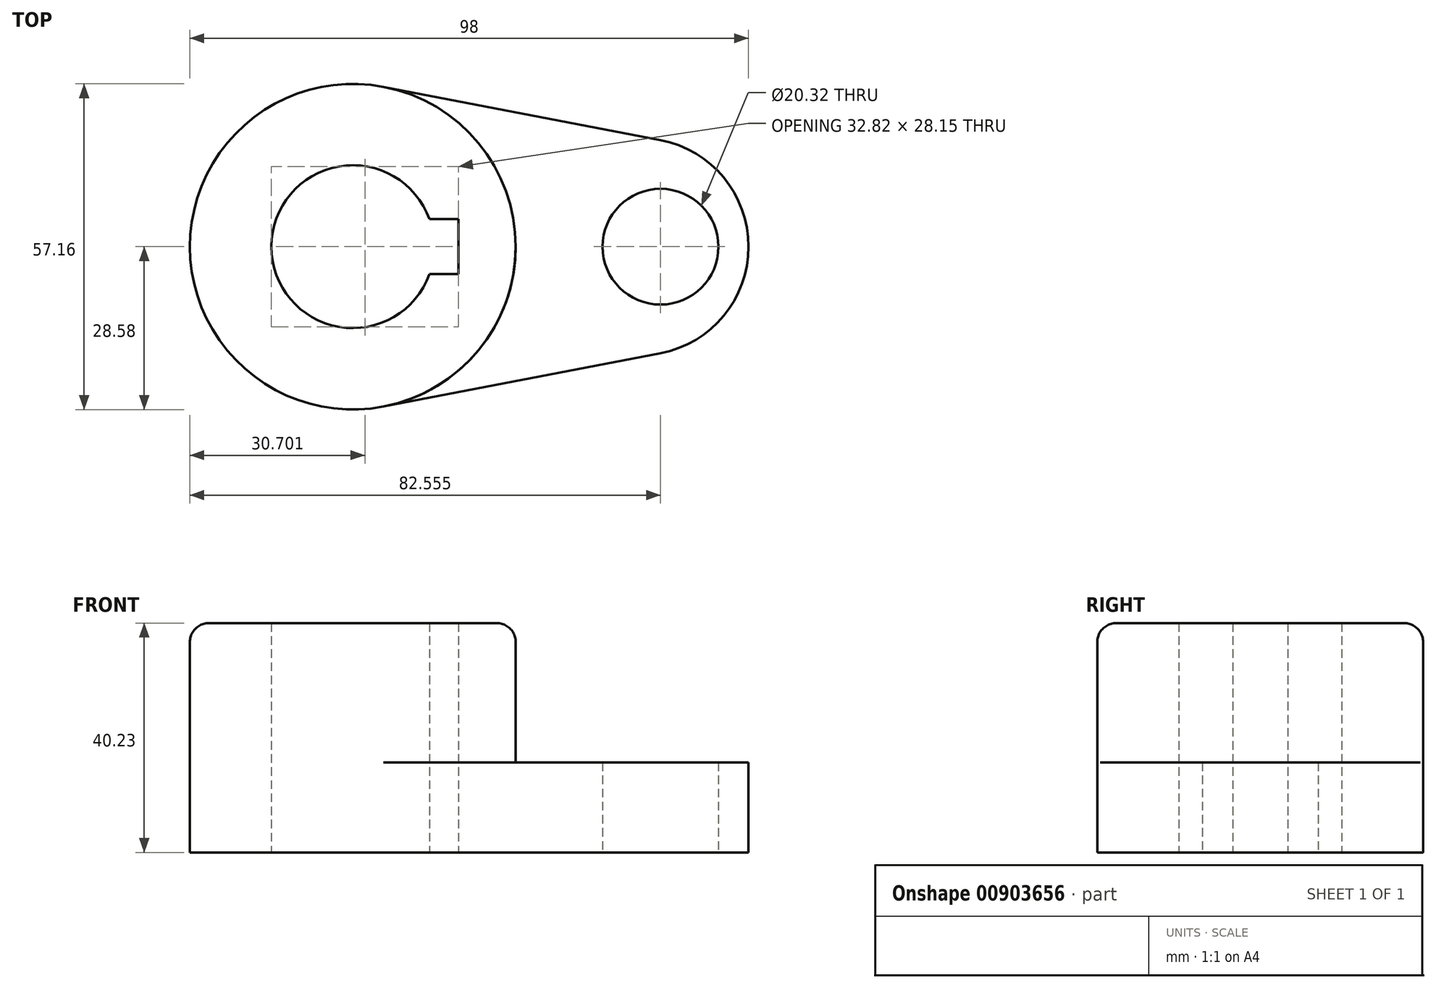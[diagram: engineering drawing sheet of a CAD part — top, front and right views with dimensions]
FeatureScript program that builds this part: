
annotation { "Feature Type Name" : "Feature", "Feature Type Description" : "" }
export const myFeature = defineFeature(function(context is Context, id is Id, definition is map)
    precondition{}
    {
        {
            var Q0;
            Q0=qCreatedBy(makeId("Top.planeOp"),FACE);
            var sketch = newSketch(context, id + "F0", { "sketchPlane" : qUnion([Q0])});
            skCircle(sketch, "E0", {"center": v(0, 0) * mm, "radius": 28.58 * mm});
            skCircle(sketch, "E1", {"center": v(53.98, 0) * mm, "radius": 10.16 * mm});
            skArc(sketch, "E2", {"start": v(13.45, 4.83) * mm, "mid": v(-14.29, 0) * mm, "end": v(13.45, -4.83) * mm});
            skLineSegment(sketch, "E3", {"start": v(14.29, 0) * mm, "end": v(18.53, 0) * mm});
            skLineSegment(sketch, "E4.bottom", {"start": v(18.53, 4.83) * mm, "end": v(13.45, 4.83) * mm});
            skLineSegment(sketch, "E4.top", {"start": v(18.53, -4.83) * mm, "end": v(13.45, -4.83) * mm});
            skLineSegment(sketch, "E4.left", {"start": v(18.53, 4.83) * mm, "end": v(18.53, -4.83) * mm});
            skPoint(sketch, "E4.middle", {"position": v(14.29, 0) * mm});
            skPoint(sketch, "E5.orphan", {"position": v(10.05, -4.83) * mm});
            skPoint(sketch, "E6.orphan", {"position": v(10.05, 4.83) * mm});
            skLineSegment(sketch, "E7", {"start": v(53.97, -18.7) * mm, "end": v(5.4, -28.06) * mm});
            skLineSegment(sketch, "E8", {"start": v(5.4, 28.06) * mm, "end": v(53.98, 18.7) * mm});
            skArc(sketch, "E9", {"start": v(53.97, -18.7) * mm, "mid": v(69.42, 0) * mm, "end": v(53.97, 18.7) * mm});
            skSolve(sketch);
        }
        {
            var Q0;
            Q0=makeQuery(id+"F0.imprint","IMPRINT",FACE,{"disambiguationData":[TD([[makeQuery(id+"F0.imprint","IMPRINT",EDGE,{"derivedFrom":sQuery(id+"F0.wireOp",EDGE,"E1")}),-1.0]])]});
            extrude(context, id + "F1", {"entities" : qUnion([Q0]), "depth" : 15.77 * mm, "offsetDistance" : 25.4 * mm});
        }
        {
            var Q0;
            Q0=makeQuery(id+"F0.imprint","IMPRINT",FACE,{"disambiguationData":[TD([[makeQuery(id+"F0.imprint","IMPRINT",EDGE,{"derivedFrom":sQuery(id+"F0.wireOp",EDGE,"E2")}),-1.0]])]});
            extrude(context, id + "F2", {"entities" : qUnion([Q0]), "operationType" : NewBodyOperationType.ADD, "depth" : 40.23 * mm, "offsetDistance" : 25.4 * mm});
        }
        {
            var Q0;
            Q0=makeQuery(id+"F2.opExtrude","CAP_EDGE",EDGE,{"disambiguationData":[OSD([sQuery(id+"F0.wireOp",EDGE,"E0")])],"isStart":false});
            fillet(context, id + "F3", {"entities" : qUnion([Q0]), "radius" : 3.3 * mm, "tangentPropagation" : true, "allowEdgeOverflow" : false});
        }
    });
